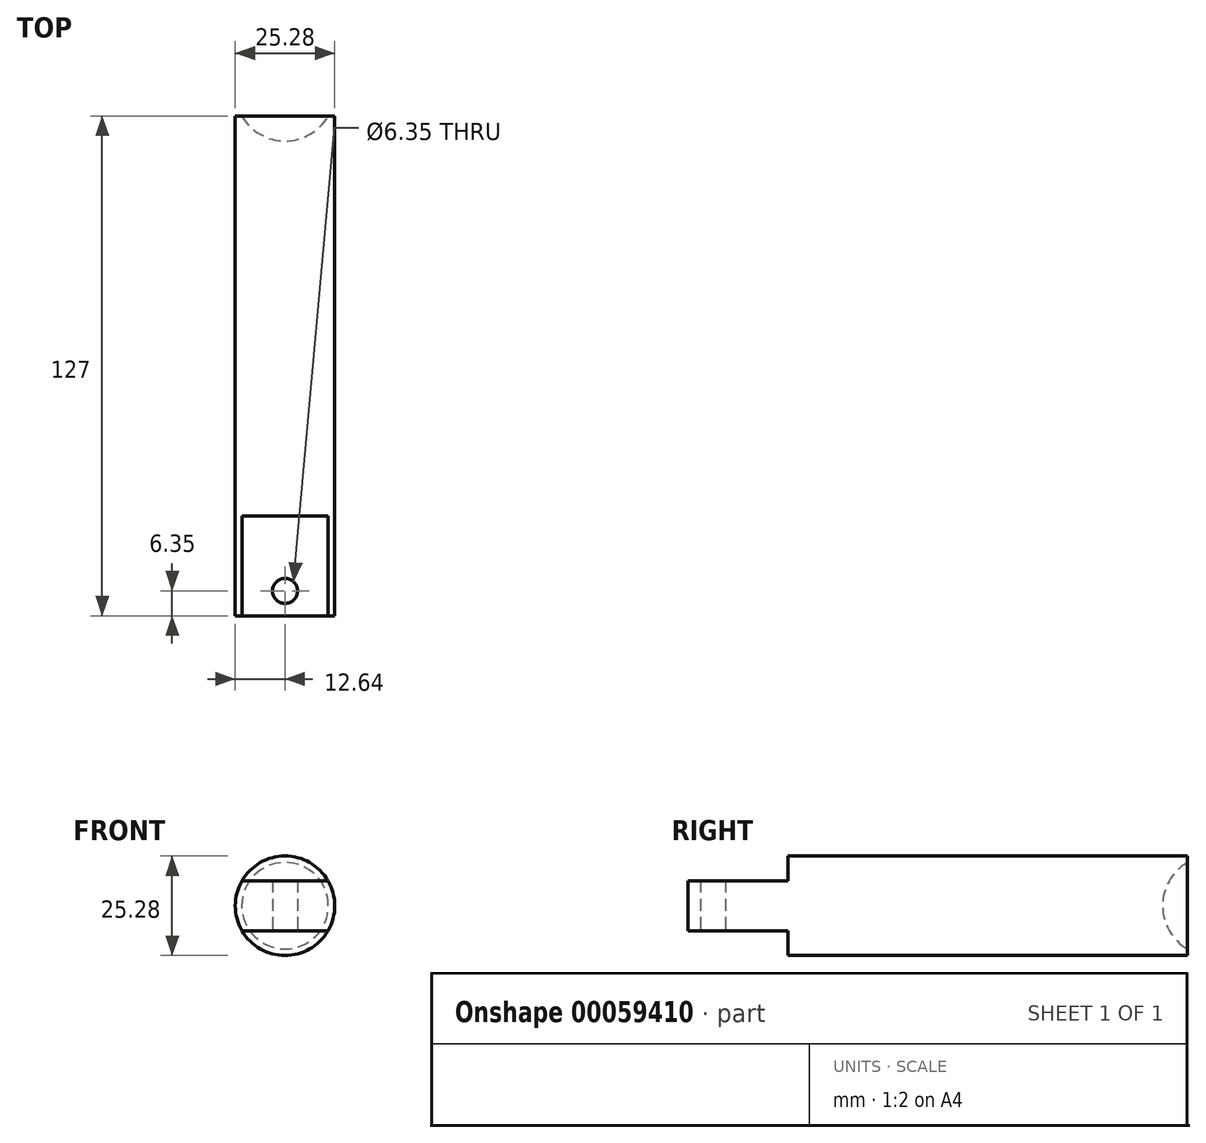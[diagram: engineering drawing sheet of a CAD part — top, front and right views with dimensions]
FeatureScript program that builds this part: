
annotation { "Feature Type Name" : "Feature", "Feature Type Description" : "" }
export const myFeature = defineFeature(function(context is Context, id is Id, definition is map)
    precondition{}
    {
        {
            var Q0;
            Q0=qCreatedBy(makeId("Front.planeOp"),FACE);
            var sketch = newSketch(context, id + "F0", { "sketchPlane" : qUnion([Q0])});
            skCircle(sketch, "E0", {"center": v(0, 0) * mm, "radius": 12.64 * mm});
            skSolve(sketch);
        }
        {
            var Q0;
            Q0=qSketchRegion(id+"F0",true);
            extrude(context, id + "F1", {"entities" : qUnion([Q0]), "oppositeDirection" : true, "depth" : 127 * mm});
        }
        {
            var Q0;
            Q0=makeQuery(id+"F1.opExtrude","CAP_FACE",FACE,{"disambiguationData":[OSD([sQuery(id+"F0.wireOp",EDGE,"E0")])],"isStart":true});
            var sketch = newSketch(context, id + "F2", { "sketchPlane" : qUnion([Q0])});
            skLineSegment(sketch, "E1.bottom", {"start": v(-19.55, -15.48) * mm, "end": v(21.41, -15.48) * mm});
            skLineSegment(sketch, "E1.top", {"start": v(-19.55, 15.7) * mm, "end": v(21.41, 15.7) * mm});
            skLineSegment(sketch, "E2", {"start": v(-19.55, -15.48) * mm, "end": v(-19.55, -6.35) * mm});
            skLineSegment(sketch, "E3", {"start": v(21.41, -6.35) * mm, "end": v(21.41, -15.48) * mm});
            skLineSegment(sketch, "E4", {"start": v(21.41, -6.35) * mm, "end": v(-19.55, -6.35) * mm});
            skLineSegment(sketch, "E5", {"start": v(-19.55, 15.7) * mm, "end": v(-19.55, 6.35) * mm});
            skLineSegment(sketch, "E6", {"start": v(21.41, 6.35) * mm, "end": v(-19.55, 6.35) * mm});
            skLineSegment(sketch, "E7", {"start": v(21.41, 6.35) * mm, "end": v(21.41, 15.7) * mm});
            skSolve(sketch);
        }
        {
            var Q0;
            Q0=qSketchRegion(id+"F2",true);
            extrude(context, id + "F3", {"entities" : qUnion([Q0]), "operationType" : NewBodyOperationType.REMOVE, "oppositeDirection" : true, "depth" : 25.4 * mm});
        }
        {
            var Q0;
            Q0=makeQuery(id+"F3.boolean.opBoolean","COPY",FACE,{"derivedFrom":makeQuery(id+"F3.opExtrude","SWEPT_FACE",FACE,{"disambiguationData":[OSD([sQuery(id+"F2.wireOp",EDGE,"E4")])]})});
            var sketch = newSketch(context, id + "F4", { "sketchPlane" : qUnion([Q0])});
            skCircle(sketch, "E8", {"center": v(0, -6.35) * mm, "radius": 3.18 * mm});
            skSolve(sketch);
        }
        {
            var Q0;
            Q0=qSketchRegion(id+"F4",true);
            extrude(context, id + "F5", {"entities" : qUnion([Q0]), "operationType" : NewBodyOperationType.REMOVE, "endBound" : BoundingType.UP_TO_NEXT, "oppositeDirection" : true, "depth" : 25.4 * mm});
        }
        {
            var Q0;
            Q0=qCreatedBy(makeId("Top.planeOp"),FACE);
            var sketch = newSketch(context, id + "F6", { "sketchPlane" : qUnion([Q0])});
            skArc(sketch, "E9", {"start": v(12.7, 133.35) * mm, "mid": v(0, 146.05) * mm, "end": v(-12.7, 133.35) * mm});
            skLineSegment(sketch, "E10", {"start": v(0, 133.35) * mm, "end": v(-12.7, 133.35) * mm});
            skLineSegment(sketch, "E11", {"start": v(0, 133.35) * mm, "end": v(12.7, 133.35) * mm});
            skSolve(sketch);
        }
        {
            var Q0;
            Q0=qSketchRegion(id+"F6",true);
            var Q1;
            Q1=sQuery(id+"F6.wireOp",EDGE,"E10");
            revolve(context, id + "F7", {"operationType" : NewBodyOperationType.REMOVE, "entities" : qUnion([Q0]), "axis" : qUnion([Q1]), "revolveType" : RevolveType.FULL, "oppositeDirection" : true});
        }
    });
